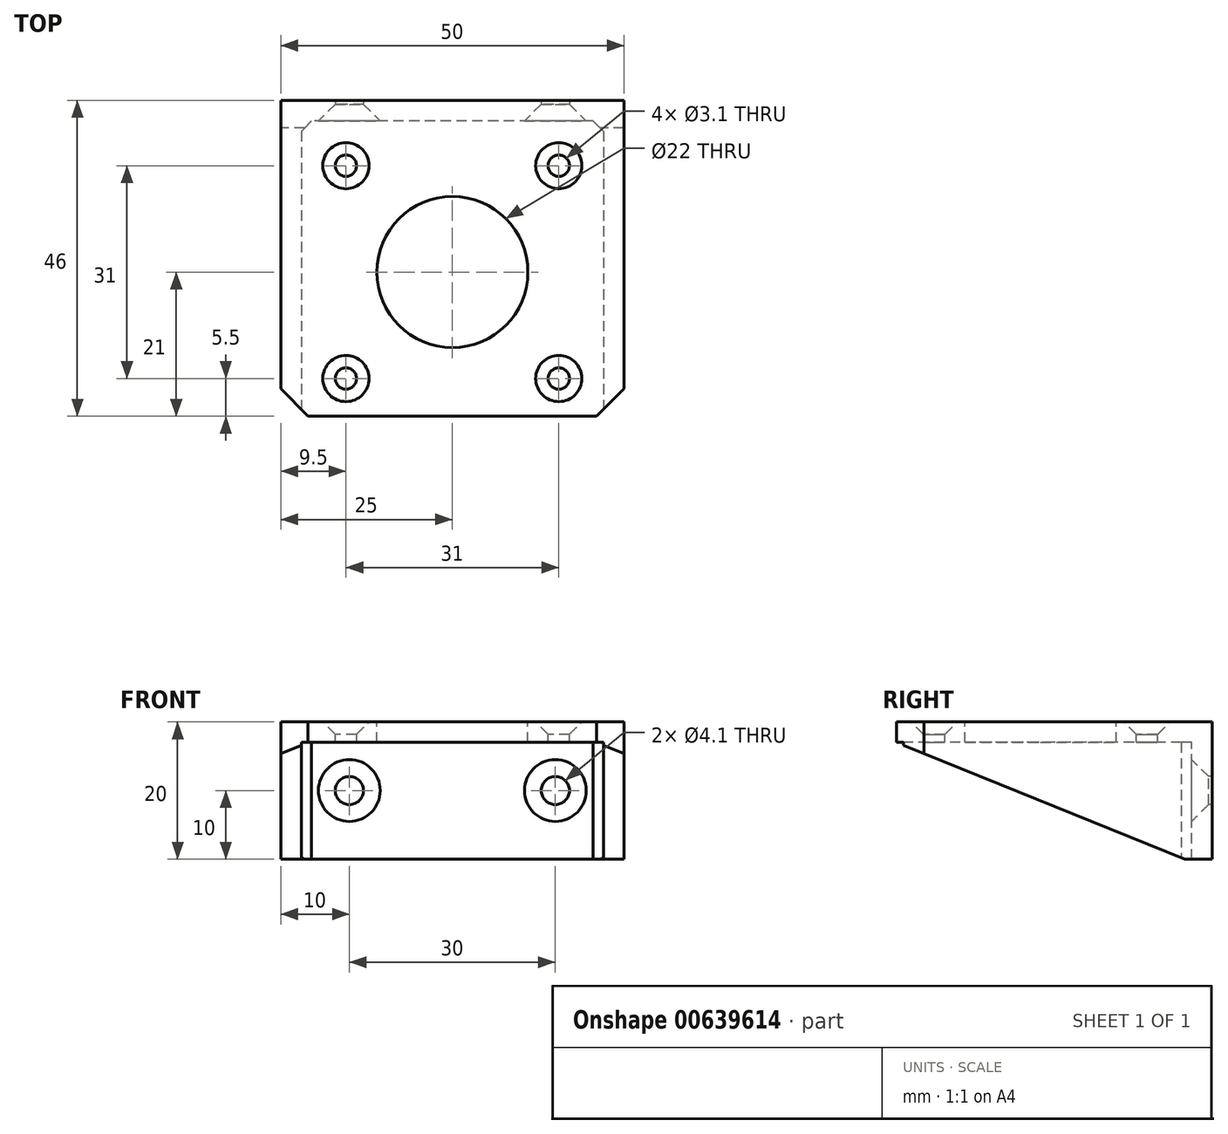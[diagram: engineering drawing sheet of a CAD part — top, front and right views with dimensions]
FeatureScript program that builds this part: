
annotation { "Feature Type Name" : "Feature", "Feature Type Description" : "" }
export const myFeature = defineFeature(function(context is Context, id is Id, definition is map)
    precondition{}
    {
        {
            var Q0;
            Q0=qCreatedBy(makeId("Top.planeOp"),FACE);
            var sketch = newSketch(context, id + "F0", { "sketchPlane" : qUnion([Q0])});
            skLineSegment(sketch, "E0.bottom", {"start": v(25, -21) * mm, "end": v(-25, -21) * mm});
            skLineSegment(sketch, "E0.top", {"start": v(25, 25) * mm, "end": v(-25, 25) * mm});
            skLineSegment(sketch, "E0.left", {"start": v(25, -21) * mm, "end": v(25, 25) * mm});
            skLineSegment(sketch, "E0.right", {"start": v(-25, -21) * mm, "end": v(-25, 25) * mm});
            skPoint(sketch, "E0.middle", {"position": v(0, 0) * mm});
            skCircle(sketch, "E1", {"center": v(0, 0) * mm, "radius": 11 * mm});
            skPoint(sketch, "E2", {"position": v(15.5, 15.5) * mm});
            skPoint(sketch, "E3.MirrorP", {"position": v(15.5, -15.5) * mm});
            skPoint(sketch, "E4.MirrorP", {"position": v(-15.5, 15.5) * mm});
            skPoint(sketch, "E5.MirrorP", {"position": v(-15.5, -15.5) * mm});
            skSolve(sketch);
        }
        {
            var Q0;
            Q0 = qSketchRegion(id + "F0", true);
            extrude(context, id + "F1", {"entities" : qUnion([Q0]), "oppositeDirection" : true, "depth" : 20 * mm, "offsetDistance" : 25 * mm});
        }
        {
            var Q0;
            Q0=makeQuery(id+"F1.opExtrude","CAP_FACE",FACE,{"disambiguationData":[OSD([sQuery(id+"F0.wireOp",EDGE,"E0.bottom"),sQuery(id+"F0.wireOp",EDGE,"E0.top"),sQuery(id+"F0.wireOp",EDGE,"E0.left"),sQuery(id+"F0.wireOp",EDGE,"E0.right"),sQuery(id+"F0.wireOp",EDGE,"E1")])],"isStart":false});
            var sketch = newSketch(context, id + "F2", { "sketchPlane" : qUnion([Q0])});
            skLineSegment(sketch, "E6.bottom", {"start": v(22, -22) * mm, "end": v(-22, -22) * mm});
            skLineSegment(sketch, "E6.top", {"start": v(22, 21) * mm, "end": v(-22, 21) * mm});
            skLineSegment(sketch, "E6.left", {"start": v(22, -22) * mm, "end": v(22, 21) * mm});
            skLineSegment(sketch, "E6.right", {"start": v(-22, -22) * mm, "end": v(-22, 21) * mm});
            skPoint(sketch, "E6.middle", {"position": v(0, 0) * mm});
            skSolve(sketch);
        }
        {
            var Q0;
            Q0 = qSketchRegion(id + "F2", true);
            var Q1;
            Q1=makeQuery(id+"F1.opExtrude","CAP_FACE",FACE,{"disambiguationData":[OSD([sQuery(id+"F0.wireOp",EDGE,"E0.bottom"),sQuery(id+"F0.wireOp",EDGE,"E0.top"),sQuery(id+"F0.wireOp",EDGE,"E0.left"),sQuery(id+"F0.wireOp",EDGE,"E0.right"),sQuery(id+"F0.wireOp",EDGE,"E1")])],"isStart":true});
            extrude(context, id + "F3", {"entities" : qUnion([Q0]), "operationType" : NewBodyOperationType.REMOVE, "endBound" : BoundingType.UP_TO_SURFACE, "oppositeDirection" : true, "depth" : 25 * mm, "endBoundEntityFace" : qUnion([Q1]), "hasOffset" : true, "offsetDistance" : 3 * mm});
        }
        {
            var Q0;
            Q0=makeQuery(id+"F1.opExtrude","CAP_EDGE",EDGE,{"disambiguationData":[OSD([sQuery(id+"F0.wireOp",EDGE,"E0.bottom")])],"isStart":false});
            chamfer(context, id + "F4", {"entities" : qUnion([Q0]), "chamferType" : ChamferType.TWO_OFFSETS, "width1" : 42 * mm, "oppositeDirection" : false, "width2" : 17 * mm, "tangentPropagation" : true});
        }
        {
            var Q0;
            Q0=sQuery(id+"F0.wireOp",VERTEX,"E2");
            var Q1;
            Q1=sQuery(id+"F0.wireOp",VERTEX,"E4.MirrorP");
            var Q2;
            Q2=sQuery(id+"F0.wireOp",VERTEX,"E5.MirrorP");
            var Q3;
            Q3=sQuery(id+"F0.wireOp",VERTEX,"E3.MirrorP");
            var Q4;
            Q4=makeQuery(id+"F1.opExtrude","SWEPT_BODY",BODY,{"disambiguationData":[OSD([sQuery(id+"F0.wireOp",EDGE,"E0.bottom"),sQuery(id+"F0.wireOp",EDGE,"E0.top"),sQuery(id+"F0.wireOp",EDGE,"E0.left"),sQuery(id+"F0.wireOp",EDGE,"E0.right"),sQuery(id+"F0.wireOp",EDGE,"E1")])]});
            hole(context, id + "F5", {"style" : HoleStyle.C_SINK, "endStyle" : HoleEndStyle.THROUGH, "standardTappedOrClearance" : lookupTablePath({ "standard" : "ISO", "size" : "3.1", "type" : "Drilled" }), "standardBlindInLast" : lookupTablePath({ "standard" : "ISO", "size" : "3.1", "type" : "Drilled" }), "holeDiameter" : 3.1 * mm, "cSinkDiameter" : 6.72 * mm, "cSinkAngle" : 90 * degree, "majorDiameter" : 5 * mm, "isTappedThrough" : true, "tappedDepth" : 12 * mm, "tapClearance" : 3, "locations" : qUnion([Q0, Q1, Q2, Q3]), "scope" : qUnion([Q4])});
        }
        {
            var Q0;
            Q0=makeQuery(id+"F1.opExtrude","SWEPT_EDGE",EDGE,{"disambiguationData":[OSD([sQuery(id+"F0.wireOp",EDGE,"E0.bottom"),sQuery(id+"F0.wireOp",EDGE,"E0.right")])]});
            var Q1;
            Q1=makeQuery(id+"F1.opExtrude","SWEPT_EDGE",EDGE,{"disambiguationData":[OSD([sQuery(id+"F0.wireOp",EDGE,"E0.bottom"),sQuery(id+"F0.wireOp",EDGE,"E0.left")])]});
            chamfer(context, id + "F6", {"entities" : qUnion([Q0, Q1]), "width" : 4 * mm, "tangentPropagation" : true});
        }
        {
            var Q0;
            Q0=makeQuery(id+"F3.boolean.opBoolean","COPY",EDGE,{"derivedFrom":makeQuery(id+"F3.opExtrude","SWEPT_EDGE",EDGE,{"disambiguationData":[OSD([sQuery(id+"F2.wireOp",EDGE,"E6.bottom"),sQuery(id+"F2.wireOp",EDGE,"E6.right")])]})});
            var Q1;
            Q1=makeQuery(id+"F3.boolean.opBoolean","COPY",EDGE,{"derivedFrom":makeQuery(id+"F3.opExtrude","SWEPT_EDGE",EDGE,{"disambiguationData":[OSD([sQuery(id+"F2.wireOp",EDGE,"E6.bottom"),sQuery(id+"F2.wireOp",EDGE,"E6.left")])]})});
            chamfer(context, id + "F7", {"entities" : qUnion([Q0, Q1]), "width" : 1.5 * mm, "tangentPropagation" : true});
        }
        {
            var Q0;
            Q0=makeQuery(id+"F3.boolean.opBoolean","COPY",FACE,{"derivedFrom":makeQuery(id+"F3.opExtrude","SWEPT_FACE",FACE,{"disambiguationData":[OSD([sQuery(id+"F2.wireOp",EDGE,"E6.bottom")])]})});
            var sketch = newSketch(context, id + "F8", { "sketchPlane" : qUnion([Q0])});
            skPoint(sketch, "E7", {"position": v(15, -10) * mm});
            skPoint(sketch, "E8.MirrorP", {"position": v(-15, -10) * mm});
            skSolve(sketch);
        }
        {
            var Q0;
            Q0=sQuery(id+"F8.wireOp",VERTEX,"E7");
            var Q1;
            Q1=sQuery(id+"F8.wireOp",VERTEX,"E8.MirrorP");
            var Q2;
            Q2=makeQuery(id+"F1.opExtrude","SWEPT_BODY",BODY,{"disambiguationData":[OSD([sQuery(id+"F0.wireOp",EDGE,"E0.bottom"),sQuery(id+"F0.wireOp",EDGE,"E0.top"),sQuery(id+"F0.wireOp",EDGE,"E0.left"),sQuery(id+"F0.wireOp",EDGE,"E0.right"),sQuery(id+"F0.wireOp",EDGE,"E1")])]});
            hole(context, id + "F9", {"style" : HoleStyle.C_SINK, "endStyle" : HoleEndStyle.THROUGH, "standardTappedOrClearance" : lookupTablePath({ "standard" : "ISO", "size" : "4.1", "type" : "Drilled" }), "standardBlindInLast" : lookupTablePath({ "standard" : "ISO", "size" : "4.1", "type" : "Drilled" }), "holeDiameter" : 4.1 * mm, "cSinkDiameter" : 9 * mm, "cSinkAngle" : 90 * degree, "majorDiameter" : 5 * mm, "isTappedThrough" : true, "tappedDepth" : 12 * mm, "tapClearance" : 3, "locations" : qUnion([Q0, Q1]), "scope" : qUnion([Q2])});
        }
    });
